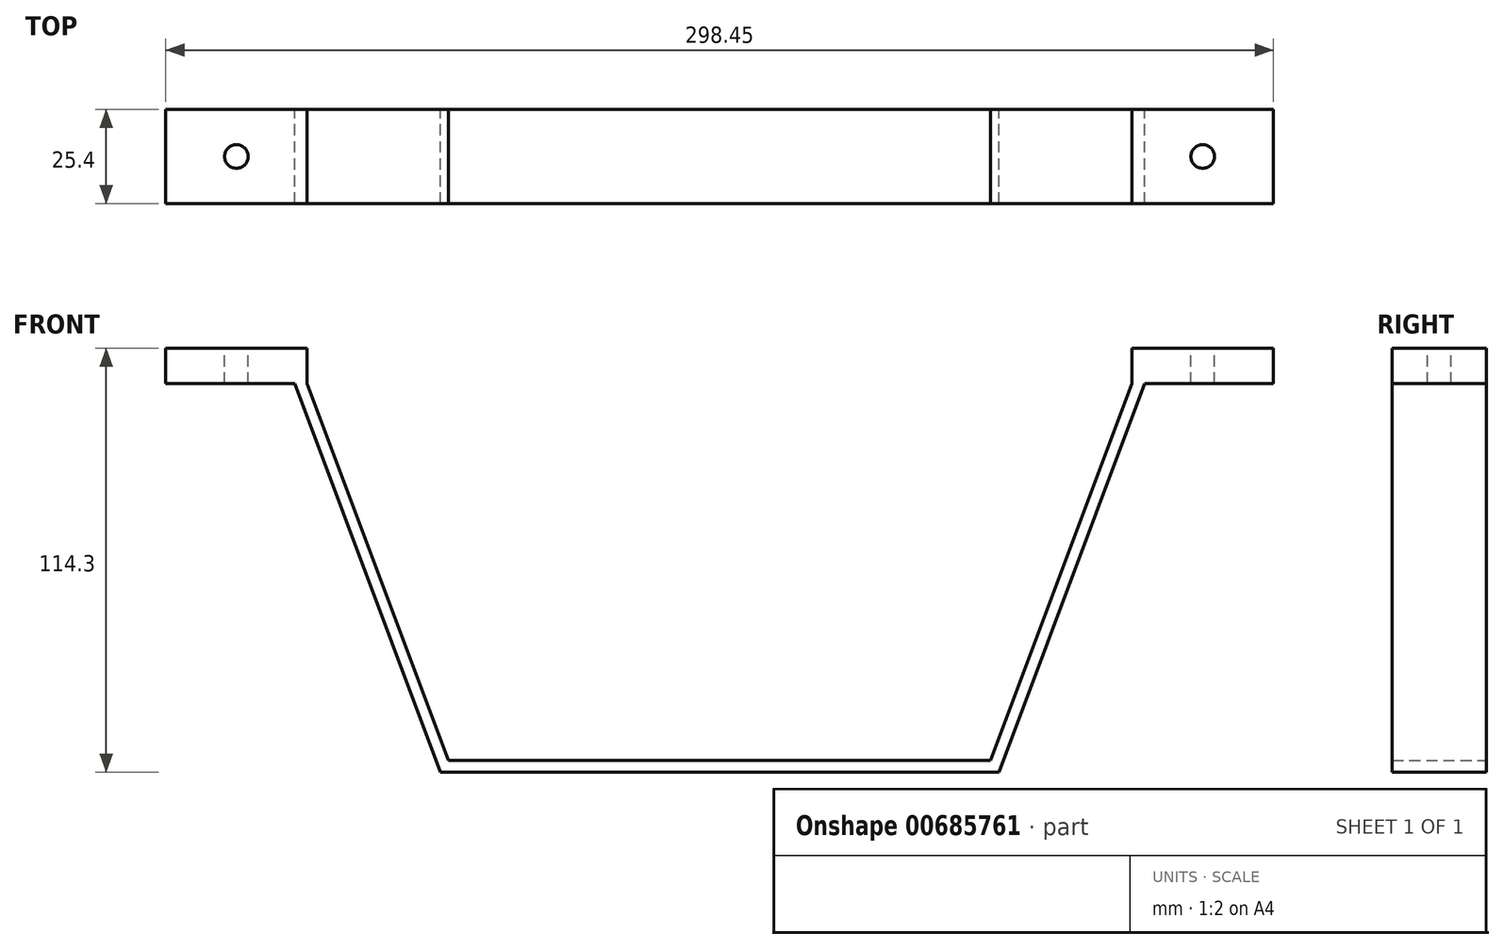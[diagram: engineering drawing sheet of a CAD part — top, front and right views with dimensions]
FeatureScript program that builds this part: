
annotation { "Feature Type Name" : "Feature", "Feature Type Description" : "" }
export const myFeature = defineFeature(function(context is Context, id is Id, definition is map)
    precondition{}
    {
        {
            var Q0;
            Q0=qCreatedBy(makeId("Front.planeOp"),FACE);
            var sketch = newSketch(context, id + "F0", { "sketchPlane" : qUnion([Q0])});
            skLineSegment(sketch, "E0.bottom", {"start": v(-106.42, 25.68) * mm, "end": v(-68.32, 25.68) * mm});
            skLineSegment(sketch, "E0.top", {"start": v(-106.42, 16.16) * mm, "end": v(-68.32, 16.16) * mm});
            skLineSegment(sketch, "E0.left", {"start": v(-106.42, 25.68) * mm, "end": v(-106.42, 16.16) * mm});
            skLineSegment(sketch, "E0.right", {"start": v(-68.32, 25.68) * mm, "end": v(-68.32, 16.16) * mm});
            skLineSegment(sketch, "E1.bottom", {"start": v(192.03, 16.16) * mm, "end": v(153.93, 16.16) * mm});
            skLineSegment(sketch, "E1.top", {"start": v(192.03, 25.68) * mm, "end": v(153.93, 25.68) * mm});
            skLineSegment(sketch, "E1.left", {"start": v(192.03, 16.16) * mm, "end": v(192.03, 25.68) * mm});
            skLineSegment(sketch, "E1.right", {"start": v(153.93, 16.16) * mm, "end": v(153.93, 25.68) * mm});
            skLineSegment(sketch, "E2", {"start": v(-30.22, -85.44) * mm, "end": v(115.83, -85.44) * mm});
            skLineSegment(sketch, "E3", {"start": v(-68.32, 16.16) * mm, "end": v(-30.22, -85.44) * mm});
            skLineSegment(sketch, "E4", {"start": v(153.93, 16.16) * mm, "end": v(115.83, -85.44) * mm});
            skLineSegment(sketch, "E5.0", {"start": v(145.69, -14.85) * mm, "end": v(118.03, -88.62) * mm});
            skLineSegment(sketch, "E5.1", {"start": v(-32.42, -88.62) * mm, "end": v(118.03, -88.62) * mm});
            skLineSegment(sketch, "E5.2", {"start": v(-60.09, -14.85) * mm, "end": v(-32.42, -88.62) * mm});
            skLineSegment(sketch, "E6", {"start": v(-58.48, -19.14) * mm, "end": v(-75.29, 25.68) * mm});
            skLineSegment(sketch, "E7", {"start": v(142.66, -22.91) * mm, "end": v(160.89, 25.68) * mm});
            skSolve(sketch);
        }
        {
            var Q0;
            {var subQ0=sQuery(id+"F0.wireOp",EDGE,"E0.left");Q0=makeQuery(id+"F0.imprint","IMPRINT",FACE,{"disambiguationData":[TD([[makeQuery(id+"F0.imprint","IMPRINT",EDGE,{"derivedFrom":subQ0}),1.0]])]});}
            var Q1;
            {var subQ0=sQuery(id+"F0.wireOp",EDGE,"E0.right");Q1=makeQuery(id+"F0.imprint","IMPRINT",FACE,{"disambiguationData":[TD([[makeQuery(id+"F0.imprint","IMPRINT",EDGE,{"derivedFrom":subQ0}),-1.0]])]});}
            var Q2;
            Q2=makeQuery(id+"F0.imprint","IMPRINT",FACE,{"disambiguationData":[TD([[makeQuery(id+"F0.imprint","IMPRINT",EDGE,{"derivedFrom":sQuery(id+"F0.wireOp",EDGE,"E2")}),-1.0]])]});
            var Q3;
            {var subQ0=sQuery(id+"F0.wireOp",EDGE,"E1.right");Q3=makeQuery(id+"F0.imprint","IMPRINT",FACE,{"disambiguationData":[TD([[makeQuery(id+"F0.imprint","IMPRINT",EDGE,{"derivedFrom":subQ0}),-1.0]])]});}
            var Q4;
            {var subQ0=sQuery(id+"F0.wireOp",EDGE,"E1.left");Q4=makeQuery(id+"F0.imprint","IMPRINT",FACE,{"disambiguationData":[TD([[makeQuery(id+"F0.imprint","IMPRINT",EDGE,{"derivedFrom":subQ0}),1.0]])]});}
            extrude(context, id + "F1", {"entities" : qUnion([Q0, Q1, Q2, Q3, Q4]), "endBound" : BoundingType.SYMMETRIC, "depth" : 25.4 * mm});
        }
        {
            var Q0;
            Q0=makeQuery(id+"F1.opExtrude","SWEPT_FACE",FACE,{"disambiguationData":[OSD([sQuery(id+"F0.wireOp",EDGE,"E0.bottom")])]});
            var sketch = newSketch(context, id + "F2", { "sketchPlane" : qUnion([Q0])});
            skPoint(sketch, "E8", {"position": v(-87.37, 0) * mm});
            skCircle(sketch, "E9", {"center": v(-87.37, 0) * mm, "radius": 3.17 * mm});
            skSolve(sketch);
        }
        {
            var Q0;
            Q0=makeQuery(id+"F2.imprint","IMPRINT",FACE,{"disambiguationData":[TD([[makeQuery(id+"F2.imprint","IMPRINT",EDGE,{"derivedFrom":sQuery(id+"F2.wireOp",EDGE,"E9")}),1.0]])]});
            extrude(context, id + "F3", {"entities" : qUnion([Q0]), "oppositeDirection" : true, "depth" : 9.52 * mm});
        }
        {
            var Q0;
            Q0=makeQuery(id+"F1.opExtrude","SWEPT_FACE",FACE,{"disambiguationData":[OSD([sQuery(id+"F0.wireOp",EDGE,"E1.top")])]});
            var sketch = newSketch(context, id + "F4", { "sketchPlane" : qUnion([Q0])});
            skPoint(sketch, "E10", {"position": v(172.98, 0) * mm});
            skCircle(sketch, "E11", {"center": v(172.98, 0) * mm, "radius": 3.18 * mm});
            skSolve(sketch);
        }
        {
            var Q0;
            Q0=makeQuery(id+"F4.imprint","IMPRINT",FACE,{"disambiguationData":[TD([[makeQuery(id+"F4.imprint","IMPRINT",EDGE,{"derivedFrom":sQuery(id+"F4.wireOp",EDGE,"E11")}),1.0]])]});
            extrude(context, id + "F5", {"entities" : qUnion([Q0]), "oppositeDirection" : true, "depth" : 9.52 * mm});
        }
    });
